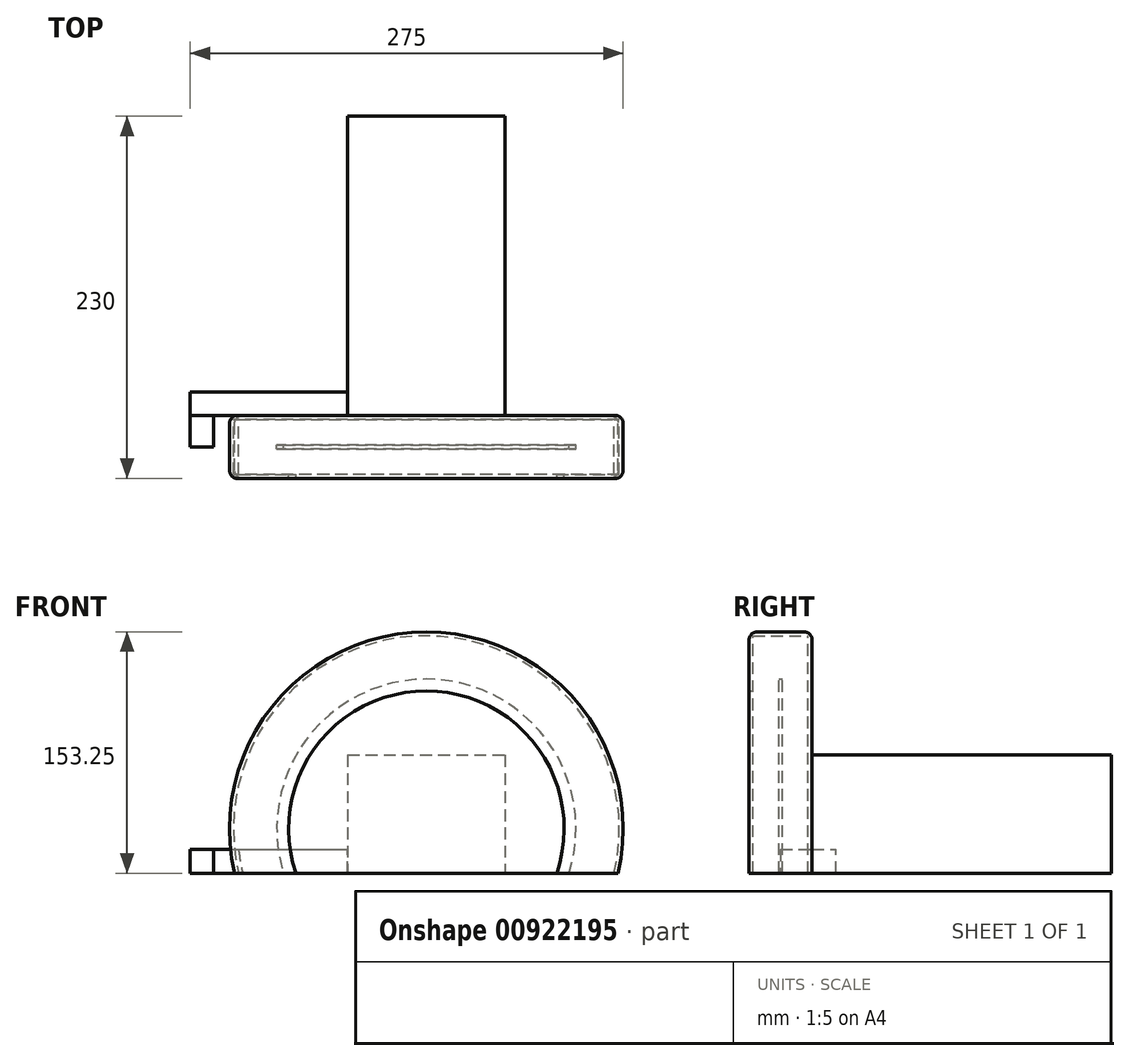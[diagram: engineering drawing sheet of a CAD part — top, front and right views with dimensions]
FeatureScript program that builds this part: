
annotation { "Feature Type Name" : "Feature", "Feature Type Description" : "" }
export const myFeature = defineFeature(function(context is Context, id is Id, definition is map)
    precondition{}
    {
        {
            var Q0;
            Q0=qCreatedBy(makeId("Front.planeOp"),FACE);
            var sketch = newSketch(context, id + "F0", { "sketchPlane" : qUnion([Q0])});
            skCircle(sketch, "E0", {"center": v(-3.03, -4.48) * mm, "radius": 95 * mm});
            skArc(sketch, "E1", {"start": v(118.74, -32.73) * mm, "mid": v(-3.03, 120.52) * mm, "end": v(-124.8, -32.73) * mm});
            skLineSegment(sketch, "E2", {"start": v(-124.8, -32.73) * mm, "end": v(118.74, -32.73) * mm});
            skLineSegment(sketch, "E3", {"start": v(-3.03, -32.73) * mm, "end": v(-3.03, -99.48) * mm, "construction": true});
            skLineSegment(sketch, "E4.bottom", {"start": v(-53.03, 42.27) * mm, "end": v(46.97, 42.27) * mm});
            skLineSegment(sketch, "E4.top", {"start": v(-53.03, -32.73) * mm, "end": v(46.97, -32.73) * mm});
            skLineSegment(sketch, "E4.left", {"start": v(-53.03, 42.27) * mm, "end": v(-53.03, -32.73) * mm});
            skLineSegment(sketch, "E4.right", {"start": v(46.97, 42.27) * mm, "end": v(46.97, -32.73) * mm});
            skArc(sketch, "E5", {"start": v(79.79, -32.73) * mm, "mid": v(-3.03, 83.02) * mm, "end": v(-85.84, -32.73) * mm});
            skSolve(sketch);
        }
        {
            var Q0;
            {var subQ4=sQuery(id+"F0.wireOp",EDGE,"E1");Q0=makeQuery(id+"F0.imprint","IMPRINT",FACE,{"disambiguationData":[TD([[makeQuery(id+"F0.imprint","IMPRINT",EDGE,{"derivedFrom":subQ4}),1.0]])]});}
            var Q1;
            {var subQ4=sQuery(id+"F0.wireOp",EDGE,"E5");Q1=makeQuery(id+"F0.imprint","IMPRINT",FACE,{"disambiguationData":[TD([[makeQuery(id+"F0.imprint","IMPRINT",EDGE,{"derivedFrom":subQ4}),-1.0]])]});}
            extrude(context, id + "F1", {"entities" : qUnion([Q0, Q1]), "endBound" : BoundingType.SYMMETRIC, "depth" : 40 * mm, "offsetDistance" : 25 * mm});
        }
        {
            var Q0;
            Q0=makeQuery(id+"F1.opExtrude","SWEPT_FACE",FACE,{"disambiguationData":[OSD([sQuery(id+"F0.wireOp",EDGE,"E5")])]});
            var Q1;
            {var subQ0=sQuery(id+"F0.wireOp",EDGE,"E2");Q1=makeQuery(id+"F1.opExtrude","SWEPT_FACE",FACE,{"disambiguationData":[OSD([subQ0]),TDD([makeQuery(id+"F0.imprint","IMPRINT",EDGE,{"disambiguationData":[TD([[makeQuery(id+"F0.imprint","INTERSECT",VERTEX,{"disambiguationData":[OD(0.0)],"derivedFrom":[subQ0,sQuery(id+"F0.wireOp",EDGE,"E5")]}),-1.0]])],"derivedFrom":subQ0}),makeQuery(id+"F0.imprint","IMPRINT",EDGE,{"disambiguationData":[TD([[makeQuery(id+"F0.imprint","INTERSECT",VERTEX,{"disambiguationData":[OD(0.0)],"derivedFrom":[sQuery(id+"F0.wireOp",EDGE,"E1"),subQ0]}),1.0]])],"derivedFrom":subQ0})])]});}
            var Q2;
            {var subQ0=sQuery(id+"F0.wireOp",EDGE,"E2");Q2=makeQuery(id+"F1.opExtrude","SWEPT_FACE",FACE,{"disambiguationData":[OSD([subQ0]),TDD([makeQuery(id+"F0.imprint","IMPRINT",EDGE,{"disambiguationData":[TD([[makeQuery(id+"F0.imprint","INTERSECT",VERTEX,{"disambiguationData":[OD(1.0)],"derivedFrom":[sQuery(id+"F0.wireOp",EDGE,"E1"),subQ0]}),-1.0]])],"derivedFrom":subQ0}),makeQuery(id+"F0.imprint","IMPRINT",EDGE,{"disambiguationData":[TD([[makeQuery(id+"F0.imprint","INTERSECT",VERTEX,{"disambiguationData":[OD(1.0)],"derivedFrom":[subQ0,sQuery(id+"F0.wireOp",EDGE,"E5")]}),1.0]])],"derivedFrom":subQ0})])]});}
            shell(context, id + "F2", {"entities" : qUnion([Q0, Q1, Q2]), "thickness" : 2.5 * mm});
        }
        {
            var Q0;
            Q0=makeQuery(id+"F0.imprint","IMPRINT",FACE,{"disambiguationData":[TD([[makeQuery(id+"F0.imprint","IMPRINT",EDGE,{"derivedFrom":sQuery(id+"F0.wireOp",EDGE,"E4.bottom")}),1.0]])]});
            var Q1;
            Q1=sQuery(id+"F0.wireOp",EDGE,"E5");
            extrude(context, id + "F3", {"entities" : qUnion([Q0]), "operationType" : NewBodyOperationType.ADD, "surfaceEntities" : qUnion([Q1]), "oppositeDirection" : true, "depth" : 20 * mm, "offsetDistance" : 25 * mm, "hasSecondDirection" : true, "secondDirectionOppositeDirection" : true, "secondDirectionDepth" : 17.5 * mm});
        }
        {
            var Q0;
            Q0=makeQuery(id+"F0.imprint","IMPRINT",FACE,{"disambiguationData":[TD([[makeQuery(id+"F0.imprint","IMPRINT",EDGE,{"derivedFrom":sQuery(id+"F0.wireOp",EDGE,"E4.bottom")}),-1.0]])]});
            extrude(context, id + "F4", {"entities" : qUnion([Q0]), "operationType" : NewBodyOperationType.ADD, "oppositeDirection" : true, "depth" : 210 * mm, "offsetDistance" : 25 * mm, "hasSecondDirection" : true, "secondDirectionOppositeDirection" : true, "secondDirectionDepth" : 17.5 * mm});
        }
        {
            var Q0;
            Q0=makeQuery(id+"F1.opExtrude","CAP_EDGE",EDGE,{"disambiguationData":[OSD([sQuery(id+"F0.wireOp",EDGE,"E1")])],"isStart":false});
            var Q1;
            Q1=makeQuery(id+"F1.opExtrude","CAP_EDGE",EDGE,{"disambiguationData":[OSD([sQuery(id+"F0.wireOp",EDGE,"E1")])],"isStart":true});
            fillet(context, id + "F5", {"entities" : qUnion([Q0, Q1]), "radius" : 5 * mm, "tangentPropagation" : true, "allowEdgeOverflow" : false});
        }
        {
            var Q0;
            {var subQ4=sQuery(id+"F0.wireOp",EDGE,"E5");Q0=makeQuery(id+"F0.imprint","IMPRINT",FACE,{"disambiguationData":[TD([[makeQuery(id+"F0.imprint","IMPRINT",EDGE,{"derivedFrom":subQ4}),-1.0]])]});}
            var Q1;
            Q1=makeQuery(id+"F0.imprint","IMPRINT",FACE,{"disambiguationData":[TD([[makeQuery(id+"F0.imprint","IMPRINT",EDGE,{"derivedFrom":sQuery(id+"F0.wireOp",EDGE,"E4.bottom")}),1.0]])]});
            var Q2;
            Q2=makeQuery(id+"F0.imprint","IMPRINT",FACE,{"disambiguationData":[TD([[makeQuery(id+"F0.imprint","IMPRINT",EDGE,{"derivedFrom":sQuery(id+"F0.wireOp",EDGE,"E4.bottom")}),-1.0]])]});
            var Q3;
            {var subQ0=sQuery(id+"F0.wireOp",EDGE,"E4.top");Q3=makeQuery(id+"F0.imprint","IMPRINT",FACE,{"disambiguationData":[TD([[makeQuery(id+"F0.imprint","IMPRINT",EDGE,{"derivedFrom":subQ0}),-1.0]])]});}
            extrude(context, id + "F6", {"entities" : qUnion([Q0, Q1, Q2, Q3]), "endBound" : BoundingType.SYMMETRIC, "depth" : 2.4 * mm, "offsetDistance" : 25 * mm});
        }
        {
            var Q0;
            Q0=makeQuery(id+"F4.opExtrude","SWEPT_FACE",FACE,{"disambiguationData":[OSD([sQuery(id+"F0.wireOp",EDGE,"E4.left")])]});
            var sketch = newSketch(context, id + "F7", { "sketchPlane" : qUnion([Q0])});
            skLineSegment(sketch, "E6.bottom", {"start": v(-20, -32.73) * mm, "end": v(-35, -32.73) * mm});
            skLineSegment(sketch, "E6.top", {"start": v(-20, -17.73) * mm, "end": v(-35, -17.73) * mm});
            skLineSegment(sketch, "E6.left", {"start": v(-20, -32.73) * mm, "end": v(-20, -17.73) * mm});
            skLineSegment(sketch, "E6.right", {"start": v(-35, -32.73) * mm, "end": v(-35, -17.73) * mm});
            skSolve(sketch);
        }
        {
            var Q0;
            Q0 = qSketchRegion(id + "F7", true);
            extrude(context, id + "F8", {"entities" : qUnion([Q0]), "operationType" : NewBodyOperationType.ADD, "depth" : 100 * mm, "offsetDistance" : 25 * mm});
        }
        {
            var Q0;
            Q0=makeQuery(id+"F8.opExtrude","SWEPT_FACE",FACE,{"disambiguationData":[OSD([sQuery(id+"F7.wireOp",EDGE,"E6.left")])]});
            var sketch = newSketch(context, id + "F9", { "sketchPlane" : qUnion([Q0])});
            skLineSegment(sketch, "E7.bottom", {"start": v(-153.03, -17.73) * mm, "end": v(-138.03, -17.73) * mm});
            skLineSegment(sketch, "E7.top", {"start": v(-153.03, -32.73) * mm, "end": v(-138.03, -32.73) * mm});
            skLineSegment(sketch, "E7.left", {"start": v(-153.03, -17.73) * mm, "end": v(-153.03, -32.73) * mm});
            skLineSegment(sketch, "E7.right", {"start": v(-138.03, -17.73) * mm, "end": v(-138.03, -32.73) * mm});
            skSolve(sketch);
        }
        {
            var Q0;
            Q0=makeQuery(id+"F9.imprint","IMPRINT",FACE,{"disambiguationData":[TD([[makeQuery(id+"F9.imprint","IMPRINT",EDGE,{"derivedFrom":sQuery(id+"F9.wireOp",EDGE,"E7.bottom")}),-1.0]])]});
            extrude(context, id + "F10", {"entities" : qUnion([Q0]), "depth" : 20 * mm, "offsetDistance" : 25 * mm});
        }
    });
